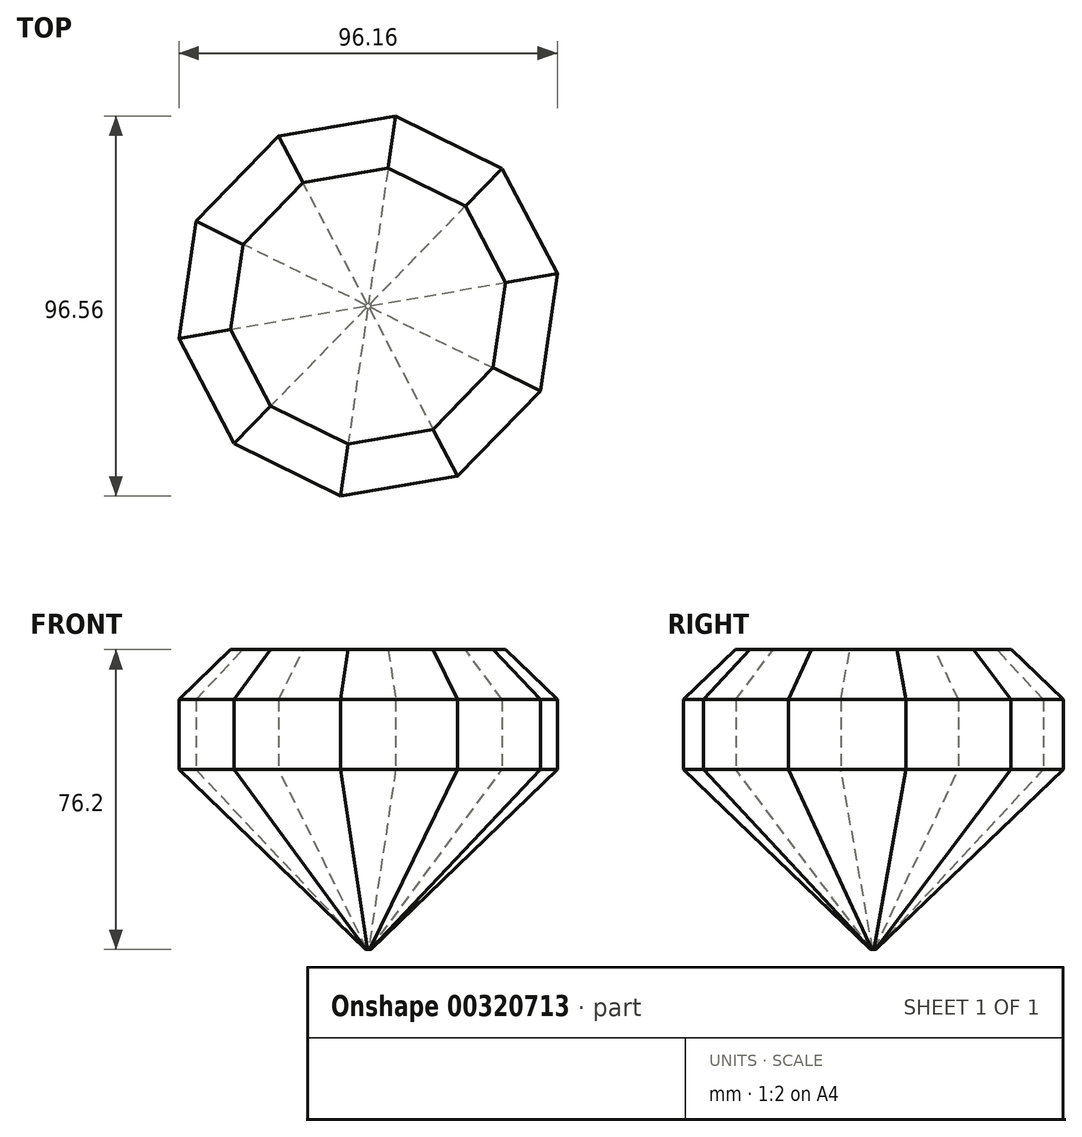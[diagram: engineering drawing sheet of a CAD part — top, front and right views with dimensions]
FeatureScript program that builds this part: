
annotation { "Feature Type Name" : "Feature", "Feature Type Description" : "" }
export const myFeature = defineFeature(function(context is Context, id is Id, definition is map)
    precondition{}
    {
        {
            var Q0;
            Q0=qCreatedBy(makeId("Top.planeOp"),FACE);
            var sketch = newSketch(context, id + "F0", { "sketchPlane" : qUnion([Q0])});
            skCircle(sketch, "E0.cCircle", {"center": v(0, 0) * mm, "radius": 48.78 * mm, "construction": true});
            skLineSegment(sketch, "E0.0", {"start": v(-43.75, 21.59) * mm, "end": v(-22.7, 43.18) * mm});
            skLineSegment(sketch, "E0.1", {"start": v(-22.7, 43.18) * mm, "end": v(7.01, 48.28) * mm});
            skLineSegment(sketch, "E0.2", {"start": v(7.01, 48.28) * mm, "end": v(34.05, 34.94) * mm});
            skLineSegment(sketch, "E0.3", {"start": v(34.05, 34.94) * mm, "end": v(48.08, 8.25) * mm});
            skLineSegment(sketch, "E0.4", {"start": v(48.08, 8.25) * mm, "end": v(43.75, -21.59) * mm});
            skLineSegment(sketch, "E0.5", {"start": v(43.75, -21.59) * mm, "end": v(22.7, -43.18) * mm});
            skLineSegment(sketch, "E0.6", {"start": v(22.7, -43.18) * mm, "end": v(-7.01, -48.28) * mm});
            skLineSegment(sketch, "E0.7", {"start": v(-7.01, -48.28) * mm, "end": v(-34.05, -34.94) * mm});
            skLineSegment(sketch, "E0.8", {"start": v(-34.05, -34.94) * mm, "end": v(-48.08, -8.25) * mm});
            skLineSegment(sketch, "E0.9", {"start": v(-48.08, -8.25) * mm, "end": v(-43.75, 21.59) * mm});
            skSolve(sketch);
        }
        {
            var Q0;
            Q0 = qSketchRegion(id + "F0", true);
            extrude(context, id + "F1", {"entities" : qUnion([Q0]), "depth" : 76.2 * mm});
        }
        {
            var Q0;
            Q0=makeQuery(id+"F1.opExtrude","CAP_EDGE",EDGE,{"disambiguationData":[OSD([sQuery(id+"F0.wireOp",EDGE,"E0.6")])],"isStart":false});
            var Q1;
            Q1=makeQuery(id+"F1.opExtrude","CAP_EDGE",EDGE,{"disambiguationData":[OSD([sQuery(id+"F0.wireOp",EDGE,"E0.5")])],"isStart":false});
            var Q2;
            Q2=makeQuery(id+"F1.opExtrude","CAP_EDGE",EDGE,{"disambiguationData":[OSD([sQuery(id+"F0.wireOp",EDGE,"E0.4")])],"isStart":false});
            var Q3;
            Q3=makeQuery(id+"F1.opExtrude","CAP_EDGE",EDGE,{"disambiguationData":[OSD([sQuery(id+"F0.wireOp",EDGE,"E0.3")])],"isStart":false});
            var Q4;
            Q4=makeQuery(id+"F1.opExtrude","CAP_EDGE",EDGE,{"disambiguationData":[OSD([sQuery(id+"F0.wireOp",EDGE,"E0.2")])],"isStart":false});
            var Q5;
            Q5=makeQuery(id+"F1.opExtrude","CAP_EDGE",EDGE,{"disambiguationData":[OSD([sQuery(id+"F0.wireOp",EDGE,"E0.1")])],"isStart":false});
            var Q6;
            Q6=makeQuery(id+"F1.opExtrude","CAP_EDGE",EDGE,{"disambiguationData":[OSD([sQuery(id+"F0.wireOp",EDGE,"E0.7")])],"isStart":false});
            var Q7;
            Q7=makeQuery(id+"F1.opExtrude","CAP_EDGE",EDGE,{"disambiguationData":[OSD([sQuery(id+"F0.wireOp",EDGE,"E0.8")])],"isStart":false});
            var Q8;
            Q8=makeQuery(id+"F1.opExtrude","CAP_EDGE",EDGE,{"disambiguationData":[OSD([sQuery(id+"F0.wireOp",EDGE,"E0.9")])],"isStart":false});
            var Q9;
            Q9=makeQuery(id+"F1.opExtrude","CAP_EDGE",EDGE,{"disambiguationData":[OSD([sQuery(id+"F0.wireOp",EDGE,"E0.0")])],"isStart":false});
            chamfer(context, id + "F2", {"entities" : qUnion([Q0, Q1, Q2, Q3, Q4, Q5, Q6, Q7, Q8, Q9]), "width" : 12.7 * mm, "tangentPropagation" : true});
        }
        {
            var Q0;
            Q0=makeQuery(id+"F1.opExtrude","CAP_EDGE",EDGE,{"disambiguationData":[OSD([sQuery(id+"F0.wireOp",EDGE,"E0.7")])],"isStart":true});
            var Q1;
            Q1=makeQuery(id+"F1.opExtrude","CAP_EDGE",EDGE,{"disambiguationData":[OSD([sQuery(id+"F0.wireOp",EDGE,"E0.6")])],"isStart":true});
            var Q2;
            Q2=makeQuery(id+"F1.opExtrude","CAP_EDGE",EDGE,{"disambiguationData":[OSD([sQuery(id+"F0.wireOp",EDGE,"E0.5")])],"isStart":true});
            var Q3;
            Q3=makeQuery(id+"F1.opExtrude","CAP_EDGE",EDGE,{"disambiguationData":[OSD([sQuery(id+"F0.wireOp",EDGE,"E0.4")])],"isStart":true});
            var Q4;
            Q4=makeQuery(id+"F1.opExtrude","CAP_EDGE",EDGE,{"disambiguationData":[OSD([sQuery(id+"F0.wireOp",EDGE,"E0.3")])],"isStart":true});
            var Q5;
            Q5=makeQuery(id+"F1.opExtrude","CAP_EDGE",EDGE,{"disambiguationData":[OSD([sQuery(id+"F0.wireOp",EDGE,"E0.2")])],"isStart":true});
            var Q6;
            Q6=makeQuery(id+"F1.opExtrude","CAP_EDGE",EDGE,{"disambiguationData":[OSD([sQuery(id+"F0.wireOp",EDGE,"E0.1")])],"isStart":true});
            var Q7;
            Q7=makeQuery(id+"F1.opExtrude","CAP_EDGE",EDGE,{"disambiguationData":[OSD([sQuery(id+"F0.wireOp",EDGE,"E0.0")])],"isStart":true});
            var Q8;
            Q8=makeQuery(id+"F1.opExtrude","CAP_EDGE",EDGE,{"disambiguationData":[OSD([sQuery(id+"F0.wireOp",EDGE,"E0.9")])],"isStart":true});
            var Q9;
            Q9=makeQuery(id+"F1.opExtrude","CAP_EDGE",EDGE,{"disambiguationData":[OSD([sQuery(id+"F0.wireOp",EDGE,"E0.8")])],"isStart":true});
            chamfer(context, id + "F3", {"entities" : qUnion([Q0, Q1, Q2, Q3, Q4, Q5, Q6, Q7, Q8, Q9]), "width" : 45.72 * mm, "tangentPropagation" : true});
        }
    });
